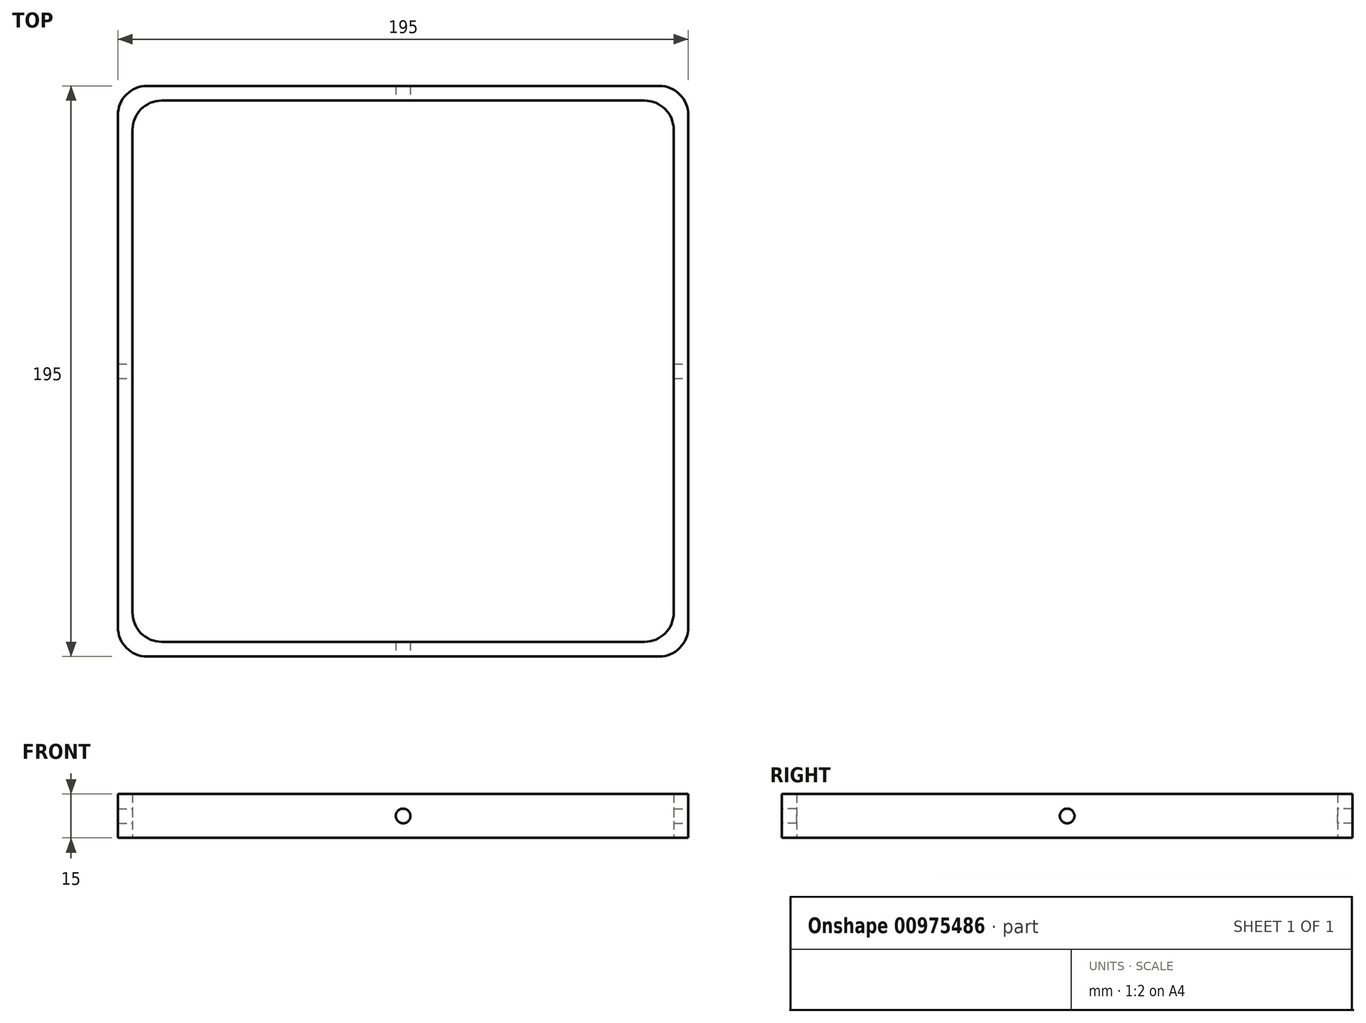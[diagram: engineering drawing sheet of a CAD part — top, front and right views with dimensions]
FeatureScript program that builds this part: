
annotation { "Feature Type Name" : "Feature", "Feature Type Description" : "" }
export const myFeature = defineFeature(function(context is Context, id is Id, definition is map)
    precondition{}
    {
        {
            var Q0;
            Q0=qCreatedBy(makeId("Top.planeOp"),FACE);
            var sketch = newSketch(context, id + "F0", { "sketchPlane" : qUnion([Q0])});
            skLineSegment(sketch, "E0.bottom", {"start": v(92.5, -92.5) * mm, "end": v(-92.5, -92.5) * mm});
            skLineSegment(sketch, "E0.top", {"start": v(92.5, 92.5) * mm, "end": v(-92.5, 92.5) * mm});
            skLineSegment(sketch, "E0.left", {"start": v(92.5, -92.5) * mm, "end": v(92.5, 92.5) * mm});
            skLineSegment(sketch, "E0.right", {"start": v(-92.5, -92.5) * mm, "end": v(-92.5, 92.5) * mm});
            skPoint(sketch, "E0.middle", {"position": v(0, 0) * mm});
            skLineSegment(sketch, "E1.0", {"start": v(97.5, -97.5) * mm, "end": v(97.5, 97.5) * mm});
            skLineSegment(sketch, "E1.1", {"start": v(97.5, -97.5) * mm, "end": v(-97.5, -97.5) * mm});
            skLineSegment(sketch, "E1.2", {"start": v(-97.5, -97.5) * mm, "end": v(-97.5, 97.5) * mm});
            skLineSegment(sketch, "E1.3", {"start": v(97.5, 97.5) * mm, "end": v(-97.5, 97.5) * mm});
            skSolve(sketch);
        }
        {
            var Q0;
            Q0=makeQuery(id+"F0.imprint","IMPRINT",FACE,{"disambiguationData":[TD([[makeQuery(id+"F0.imprint","IMPRINT",EDGE,{"derivedFrom":sQuery(id+"F0.wireOp",EDGE,"E0.bottom")}),1.0]])]});
            extrude(context, id + "F1", {"entities" : qUnion([Q0]), "depth" : 15 * mm, "offsetDistance" : 25 * mm});
        }
        {
            var Q0;
            Q0=makeQuery(id+"F1.opExtrude","SWEPT_EDGE",EDGE,{"disambiguationData":[OSD([sQuery(id+"F0.wireOp",EDGE,"E1.1"),sQuery(id+"F0.wireOp",EDGE,"E1.2")])]});
            var Q1;
            Q1=makeQuery(id+"F1.opExtrude","SWEPT_EDGE",EDGE,{"disambiguationData":[OSD([sQuery(id+"F0.wireOp",EDGE,"E1.0"),sQuery(id+"F0.wireOp",EDGE,"E1.1")])]});
            var Q2;
            Q2=makeQuery(id+"F1.opExtrude","SWEPT_EDGE",EDGE,{"disambiguationData":[OSD([sQuery(id+"F0.wireOp",EDGE,"E0.top"),sQuery(id+"F0.wireOp",EDGE,"E0.left")])]});
            var Q3;
            Q3=makeQuery(id+"F1.opExtrude","SWEPT_EDGE",EDGE,{"disambiguationData":[OSD([sQuery(id+"F0.wireOp",EDGE,"E1.2"),sQuery(id+"F0.wireOp",EDGE,"E1.3")])]});
            var Q4;
            Q4=makeQuery(id+"F1.opExtrude","SWEPT_EDGE",EDGE,{"disambiguationData":[OSD([sQuery(id+"F0.wireOp",EDGE,"E1.0"),sQuery(id+"F0.wireOp",EDGE,"E1.3")])]});
            var Q5;
            Q5=makeQuery(id+"F1.opExtrude","SWEPT_EDGE",EDGE,{"disambiguationData":[OSD([sQuery(id+"F0.wireOp",EDGE,"E0.bottom"),sQuery(id+"F0.wireOp",EDGE,"E0.left")])]});
            var Q6;
            Q6=makeQuery(id+"F1.opExtrude","SWEPT_EDGE",EDGE,{"disambiguationData":[OSD([sQuery(id+"F0.wireOp",EDGE,"E0.bottom"),sQuery(id+"F0.wireOp",EDGE,"E0.right")])]});
            var Q7;
            Q7=makeQuery(id+"F1.opExtrude","SWEPT_EDGE",EDGE,{"disambiguationData":[OSD([sQuery(id+"F0.wireOp",EDGE,"E0.top"),sQuery(id+"F0.wireOp",EDGE,"E0.right")])]});
            fillet(context, id + "F2", {"entities" : qUnion([Q0, Q1, Q2, Q3, Q4, Q5, Q6, Q7]), "radius" : 10 * mm, "tangentPropagation" : true, "allowEdgeOverflow" : false});
        }
        {
            var Q0;
            Q0=makeQuery(id+"F1.opExtrude","SWEPT_FACE",FACE,{"disambiguationData":[OSD([sQuery(id+"F0.wireOp",EDGE,"E1.1")])]});
            var sketch = newSketch(context, id + "F3", { "sketchPlane" : qUnion([Q0])});
            skLineSegment(sketch, "E2", {"start": v(-87.5, 7.5) * mm, "end": v(87.5, 7.5) * mm, "construction": true});
            skCircle(sketch, "E3", {"center": v(0, 7.5) * mm, "radius": 2.5 * mm});
            skSolve(sketch);
        }
        {
            var Q0;
            Q0 = qSketchRegion(id + "F3", true);
            extrude(context, id + "F4", {"entities" : qUnion([Q0]), "operationType" : NewBodyOperationType.REMOVE, "endBound" : BoundingType.THROUGH_ALL, "oppositeDirection" : true, "depth" : 25 * mm, "offsetDistance" : 25 * mm});
        }
        {
            var Q0;
            Q0=makeQuery(id+"F1.opExtrude","SWEPT_FACE",FACE,{"disambiguationData":[OSD([sQuery(id+"F0.wireOp",EDGE,"E1.0")])]});
            var sketch = newSketch(context, id + "F5", { "sketchPlane" : qUnion([Q0])});
            skLineSegment(sketch, "E4", {"start": v(-87.5, 7.5) * mm, "end": v(87.5, 7.5) * mm, "construction": true});
            skCircle(sketch, "E5", {"center": v(0, 7.5) * mm, "radius": 2.5 * mm});
            skSolve(sketch);
        }
        {
            var Q0;
            Q0 = qSketchRegion(id + "F5", true);
            extrude(context, id + "F6", {"entities" : qUnion([Q0]), "operationType" : NewBodyOperationType.REMOVE, "endBound" : BoundingType.THROUGH_ALL, "oppositeDirection" : true, "depth" : 25 * mm, "offsetDistance" : 25 * mm});
        }
    });
